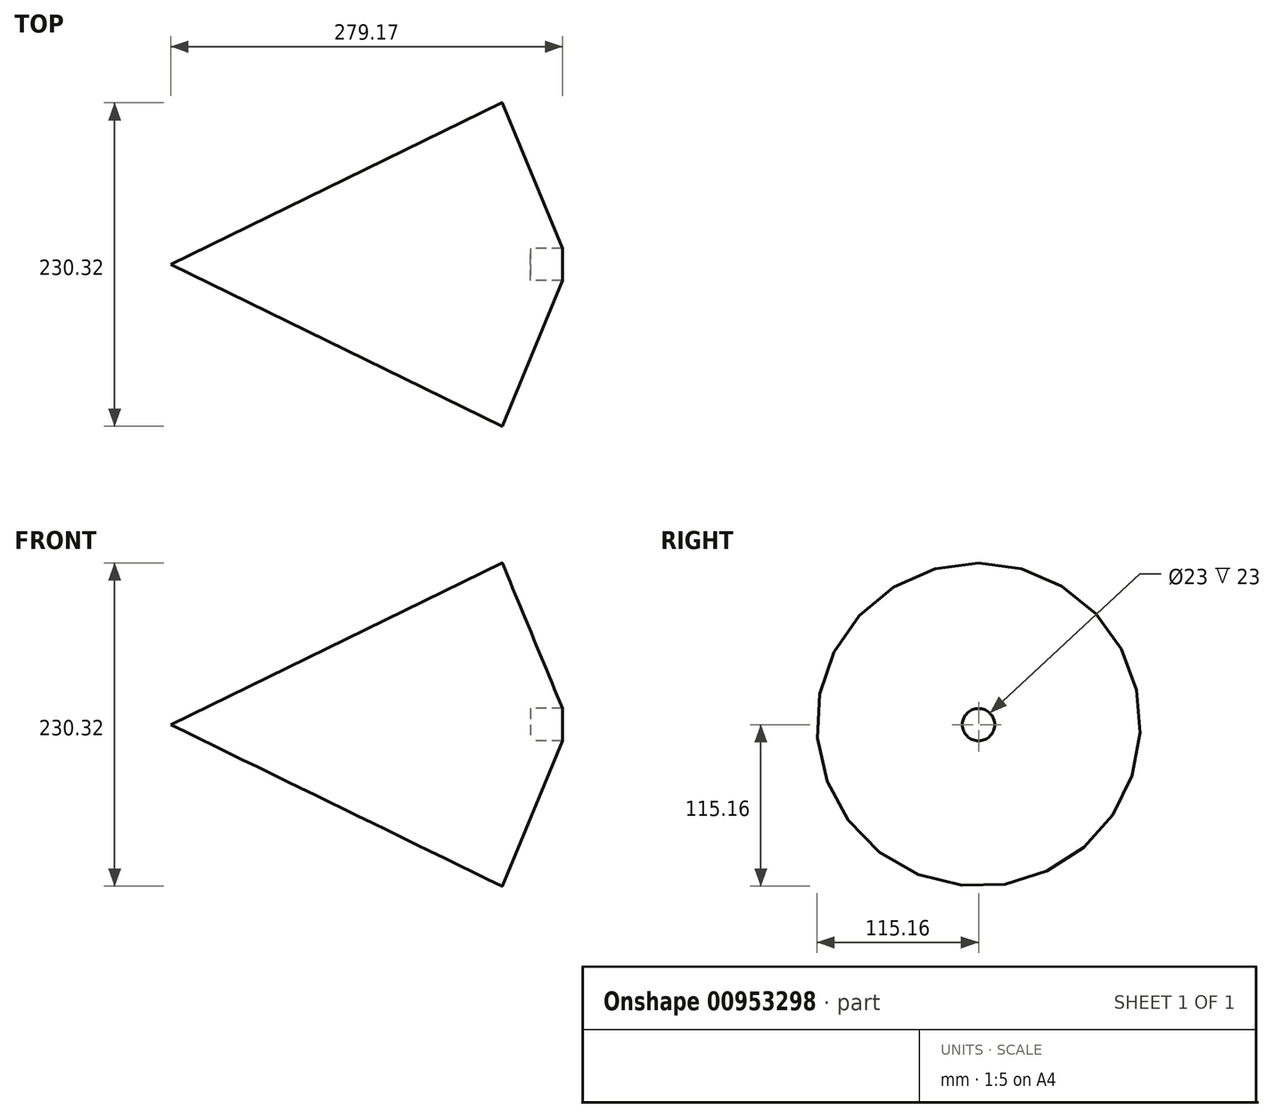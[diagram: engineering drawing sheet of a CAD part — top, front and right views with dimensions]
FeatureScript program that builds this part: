
annotation { "Feature Type Name" : "Feature", "Feature Type Description" : "" }
export const myFeature = defineFeature(function(context is Context, id is Id, definition is map)
    precondition{}
    {
        {
            var Q0;
            Q0=qCreatedBy(makeId("Front.planeOp"),FACE);
            var sketch = newSketch(context, id + "F0", { "sketchPlane" : qUnion([Q0])});
            skLineSegment(sketch, "E0", {"start": v(0, 0) * mm, "end": v(236.1, 115.15) * mm});
            skLineSegment(sketch, "E1", {"start": v(0, 0) * mm, "end": v(184.58, 0) * mm, "construction": true});
            skLineSegment(sketch, "E2", {"start": v(236.26, 115.09) * mm, "end": v(279.17, 11.5) * mm});
            skLineSegment(sketch, "E3", {"start": v(279.17, 11.5) * mm, "end": v(256.17, 11.5) * mm});
            skLineSegment(sketch, "E4", {"start": v(256.17, 11.5) * mm, "end": v(256.17, 0) * mm});
            skLineSegment(sketch, "E5", {"start": v(0, 0) * mm, "end": v(256.17, 0) * mm});
            skPoint(sketch, "E6.visualSharp", {"position": v(236.21, 115.2) * mm});
            skArc(sketch, "E6.filletArc", {"start": v(236.26, 115.09) * mm, "mid": v(236.2, 115.16) * mm, "end": v(236.1, 115.15) * mm});
            skSolve(sketch);
        }
        {
            var Q0;
            Q0=qSketchRegion(id+"F0",true);
            var Q1;
            Q1=sQuery(id+"F0.wireOp",EDGE,"E5");
            revolve(context, id + "F1", {"surfaceOperationType" : NewSurfaceOperationType.NEW, "entities" : qUnion([Q0]), "axis" : qUnion([Q1]), "revolveType" : RevolveType.FULL});
        }
    });
